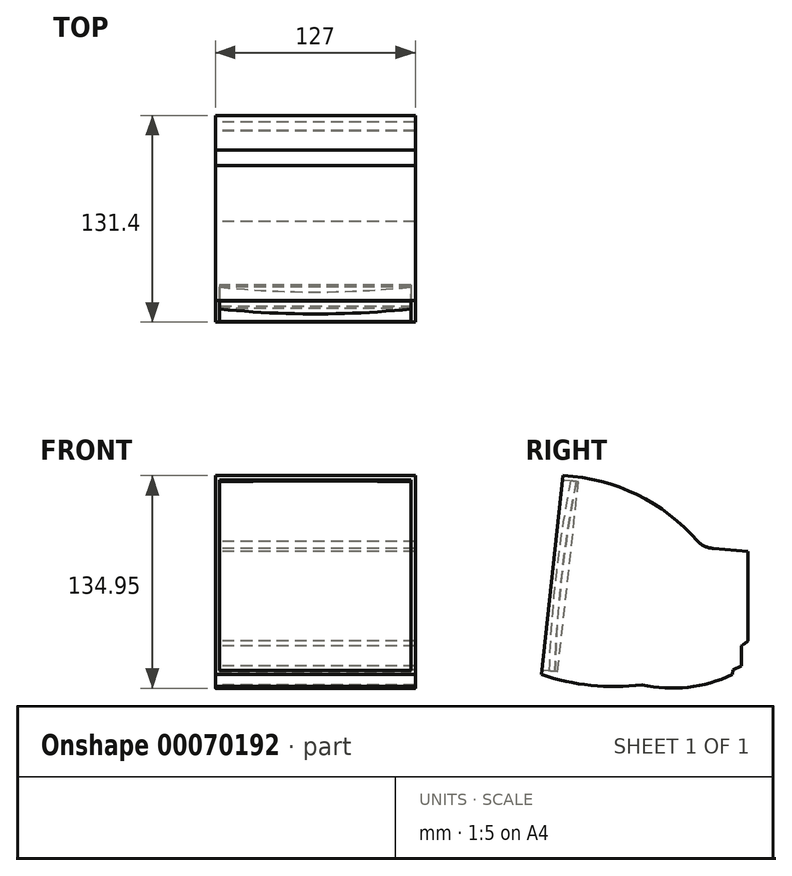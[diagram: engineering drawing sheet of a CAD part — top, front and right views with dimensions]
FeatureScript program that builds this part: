
annotation { "Feature Type Name" : "Feature", "Feature Type Description" : "" }
export const myFeature = defineFeature(function(context is Context, id is Id, definition is map)
    precondition{}
    {
        {
            var Q0;
            Q0=qCreatedBy(makeId("Right.planeOp"),FACE);
            var sketch = newSketch(context, id + "F0", { "sketchPlane" : qUnion([Q0])});
            skLineSegment(sketch, "E0", {"start": v(-45.3, -15.04) * mm, "end": v(-31.45, 111.2) * mm});
            skArc(sketch, "E1", {"start": v(54.1, 69.58) * mm, "mid": v(15.58, 99.14) * mm, "end": v(-31.45, 111.2) * mm});
            skLineSegment(sketch, "E2", {"start": v(81.8, -9.58) * mm, "end": v(76.3, -12.28) * mm});
            skLineSegment(sketch, "E3", {"start": v(76.3, -12.28) * mm, "end": v(75.99, -15.13) * mm});
            skArc(sketch, "E4", {"start": v(-45.3, -15.04) * mm, "mid": v(-13.7, -21.99) * mm, "end": v(18.66, -21.54) * mm});
            skArc(sketch, "E5", {"start": v(18.66, -21.54) * mm, "mid": v(47.87, -23.2) * mm, "end": v(75.99, -15.13) * mm});
            skArc(sketch, "E6", {"start": v(54.1, 69.58) * mm, "mid": v(58.6, 66.31) * mm, "end": v(64, 65.07) * mm});
            skLineSegment(sketch, "E7", {"start": v(86.09, 63.16) * mm, "end": v(64, 65.07) * mm});
            skLineSegment(sketch, "E8", {"start": v(86.09, 63.16) * mm, "end": v(86.09, 6.22) * mm});
            skLineSegment(sketch, "E9", {"start": v(81.8, -9.58) * mm, "end": v(81.8, 3.07) * mm});
            skLineSegment(sketch, "E10.bottom", {"start": v(-43.66, 0) * mm, "end": v(-38.2, 0) * mm});
            skLineSegment(sketch, "E10.top", {"start": v(-44.23, -5.17) * mm, "end": v(-38.77, -5.17) * mm});
            skLineSegment(sketch, "E10.left", {"start": v(-43.66, 0) * mm, "end": v(-44.23, -5.17) * mm});
            skLineSegment(sketch, "E10.right", {"start": v(-38.2, 0) * mm, "end": v(-38.77, -5.17) * mm});
            skArc(sketch, "E11.trimOffspring", {"start": v(81.8, 3.07) * mm, "mid": v(83.96, 4.63) * mm, "end": v(86.09, 6.22) * mm});
            skSolve(sketch);
        }
        {
            var Q0;
            {var subQ4=sQuery(id+"F0.wireOp",EDGE,"E0");Q0=makeQuery(id+"F0.imprint","IMPRINT",FACE,{"disambiguationData":[TD([[makeQuery(id+"F0.imprint","IMPRINT",EDGE,{"derivedFrom":subQ4}),-1.0]])]});}
            var Q1;
            Q1=makeQuery(id+"F0.imprint","IMPRINT",FACE,{"disambiguationData":[TD([[makeQuery(id+"F0.imprint","IMPRINT",EDGE,{"derivedFrom":sQuery(id+"F0.wireOp",EDGE,"E10.bottom")}),-1.0]])]});
            extrude(context, id + "F1", {"entities" : qUnion([Q0, Q1]), "depth" : 63.5 * mm, "hasSecondDirection" : true, "secondDirectionOppositeDirection" : true, "secondDirectionDepth" : 63.5 * mm});
        }
        {
            var Q0;
            Q0=makeQuery(id+"F1.opExtrude","SWEPT_FACE",FACE,{"disambiguationData":[OSD([sQuery(id+"F0.wireOp",EDGE,"E0")])]});
            var sketch = newSketch(context, id + "F2", { "sketchPlane" : qUnion([Q0])});
            skLineSegment(sketch, "E12.0", {"start": v(60.7, 104.33) * mm, "end": v(-60.7, 104.33) * mm});
            skLineSegment(sketch, "E12.1", {"start": v(60.7, -17.15) * mm, "end": v(60.7, 104.33) * mm});
            skLineSegment(sketch, "E12.2", {"start": v(-60.7, -17.15) * mm, "end": v(60.7, -17.15) * mm});
            skLineSegment(sketch, "E12.3", {"start": v(-60.7, 104.33) * mm, "end": v(-60.7, -17.15) * mm});
            skSolve(sketch);
        }
        {
            var Q0;
            Q0=makeQuery(id+"F2.imprint","IMPRINT",FACE,{"disambiguationData":[TD([[makeQuery(id+"F2.imprint","IMPRINT",EDGE,{"derivedFrom":sQuery(id+"F2.wireOp",EDGE,"E12.0")}),1.0]])]});
            extrude(context, id + "F3", {"entities" : qUnion([Q0]), "operationType" : NewBodyOperationType.REMOVE, "oppositeDirection" : true, "depth" : 10.16 * mm});
        }
        {
            var Q0;
            Q0=makeQuery(id+"F3.boolean.opBoolean","COPY",FACE,{"derivedFrom":makeQuery(id+"F3.opExtrude","SWEPT_FACE",FACE,{"disambiguationData":[OSD([sQuery(id+"F2.wireOp",EDGE,"E12.0")])]})});
            cPlane(context, id + "F4", {"entities" : qUnion([Q0]), "cplaneType" : CPlaneType.OFFSET, "offset" : 63.28 * mm, "width" : 152.4 * mm, "height" : 152.4 * mm});
        }
        {
            var Q0;
            Q0=qCreatedBy(id+"F4.planeOp",FACE);
            var sketch = newSketch(context, id + "F5", { "sketchPlane" : qUnion([Q0])});
            skLineSegment(sketch, "E13.0", {"start": v(-63.11, 37.3) * mm, "end": v(63.11, 37.3) * mm});
            skArc(sketch, "E14", {"start": v(63.11, 37.3) * mm, "mid": v(0, 40.7) * mm, "end": v(-63.11, 37.3) * mm});
            skLineSegment(sketch, "E15", {"start": v(0, -546.04) * mm, "end": v(119.31, -546.04) * mm});
            skLineSegment(sketch, "E16", {"start": v(0, -546.04) * mm, "end": v(0, -850.3) * mm});
            skLineSegment(sketch, "E17", {"start": v(0, -850.3) * mm, "end": v(129.77, -850.3) * mm});
            skLineSegment(sketch, "E18", {"start": v(0, -850.3) * mm, "end": v(0, -1181.9) * mm});
            skLineSegment(sketch, "E19", {"start": v(0, -1181.9) * mm, "end": v(99.87, -1181.9) * mm});
            skLineSegment(sketch, "E20", {"start": v(0, -698.17) * mm, "end": v(120.64, -698.17) * mm});
            skLineSegment(sketch, "E21.0", {"start": v(-60.7, 33.24) * mm, "end": v(60.7, 33.24) * mm});
            skSolve(sketch);
        }
        {
            var Q0;
            Q0=makeQuery(id+"F5.imprint","IMPRINT",FACE,{"disambiguationData":[TD([[makeQuery(id+"F5.imprint","IMPRINT",EDGE,{"derivedFrom":sQuery(id+"F5.wireOp",EDGE,"E14")}),1.0]])]});
            var Q1;
            Q1=sQuery(id+"F5.wireOp",EDGE,"E20");
            revolve(context, id + "F6", {"operationType" : NewBodyOperationType.ADD, "surfaceOperationType" : NewSurfaceOperationType.NEW, "entities" : qUnion([Q0]), "axis" : qUnion([Q1]), "revolveType" : RevolveType.TWO_DIRECTIONS, "angle" : 4.64 * degree, "angleBack" : 355.04 * degree});
        }
    });
